# Revit family: Shower-Valve_Trim-KOHLER-MODULO-K-97366T_1
name_source: partatom
category: Plumbing Fixtures
revit_build: Autodesk Revit 2017 (Build: 20160225_1515(x64)
units: mm (PartAtom-declared; Revit-internal decimal feet)

## family parameters
Cut with Voids When Loaded = No
Host = Face
OmniClass Number = 23.31.11.00
OmniClass Title = Faucets
Part Type = Normal
Room Calculation Point = No
Round Connector Dimension = Use Diameter
Shared = No

## types (5) — shared parameters
ADA Compliant = No
Assembly Code = D2010
CW Connection = Yes
Cold Water Inlet = Cold Water Inlet
Date Modified = 05/12/2021
Description = Smart Fitting Spool Series Smart Fitting In-Wall Bathtub Spool and Panel Ai Fei
Drain Included = No
Flow Rate = 0 GPM
HW Connection = Yes
Handle Clearance = 3 3/8"
Height = 7 1/8"
Hot Water Inlet = Hot Water Inlet
Length = 3 7/16"
Manufacturer = KOHLER Co.
Master Format 2014 = 22 41 39
Master Format 2014 Name = Residential Faucets, Supplies, and Trim
Material = Premium Metal Construction
Pressure = 0.00 psi
Product Name = MODULO
Tempered Water Outlet 1 = Tempered Water Outlet 1
Tempered Water Outlet 2 = Tempered Water Outlet 2
URL = http://www.kohler.com.cn
Vent Connection = No
Waste Connection = No
Waste Water Outlet = Waste Water Outlet
WaterSense Certified = No
Width = 7 1/8"

## per-type parameters (varying)
| type | Default Elevation | Finish | Model | Product Documentation Link | Product Page URL | Type |
| CP-Polished Chrome | 42" | Kohler-Metal-CP-Polished_Chrome | K-97366T-4-CP |  |  | 1 |
| TT-Titanium Silver | 36" | Kohler-Metal-TT-Titanium_Silver | K-97366T-4-TT | https://files.kohler.com.cn | https://www.kohler.com.cn | 2 |
| B4, CP-Polished Chrome | 42" | Kohler-Metal-CP-Polished_Chrome | K-97366T-B4-CP | https://files.kohler.com.cn | https://www.kohler.com.cn | 3 |
| B4, TT-Silver Titanium | 42" | Kohler-Metal-TT-Titanium_Silver | K-97366T-B4-TT |  |  | 4 |
| B4, RGD-Rose Gold | 42" | Kohler-Metal-RGD-Rose_Gold | K-97366T-B4-RGD | https://files.kohler.com.cn | https://www.kohler.com.cn | 5 |

## geometry (parser evidence)
native form markers: Sweep x5
no freeform markers — native parametric forms only
